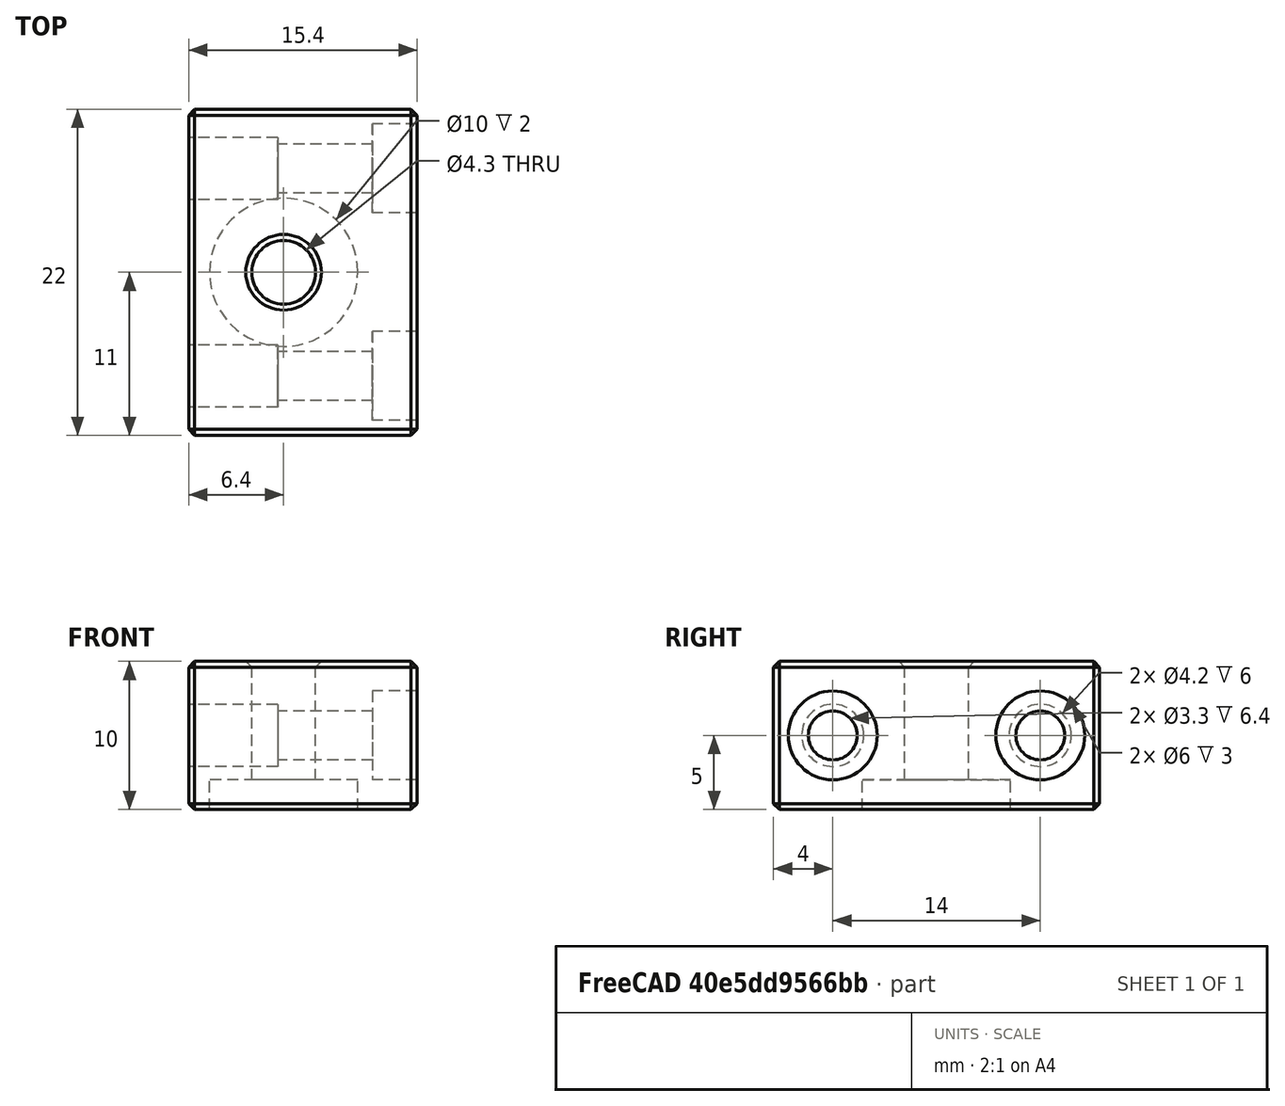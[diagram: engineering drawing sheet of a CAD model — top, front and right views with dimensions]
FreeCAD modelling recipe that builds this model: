
FCSTD DOCUMENT  (FreeCAD 0.18R16146 (Git))
Label: carrier-CF-adjust-block
License: Other
LicenseURL: GPL3
objects: Part::Cylinder×8, Part::Cut×5, Part::MultiFuse×3, Part::Box×1, Part::Chamfer×1
note: 18 computed .brp shape members not serialized (recipe doc carries the construction recipe); baked Part::Feature solids carry a one-line shape summary decoded from their .brp

FEATURE [Part::Box] Box  label="Cube"
  AttacherType = Attacher::AttachEngine3D
  Height = 10
  Length = 15.4
  Placement = pos=(-6.4,-11,0) rot=(0,0,1;0rad)
  Width = 22
FEATURE [Part::Cylinder] Cylinder
  Angle = 360
  AttacherType = Attacher::AttachEngine3D
  Height = 10
  Radius = 2.15
FEATURE [Part::Cylinder] Cylinder001
  Angle = 360
  AttacherType = Attacher::AttachEngine3D
  Height = 2
  Radius = 5
FEATURE [Part::Cylinder] Cylinder002
  Angle = 360
  AttacherType = Attacher::AttachEngine3D
  Height = 16
  Placement = pos=(9,-7,5) rot=(0,1,0;4.71239rad)
  Radius = 1.65
FEATURE [Part::Cylinder] Cylinder003
  Angle = 360
  AttacherType = Attacher::AttachEngine3D
  Height = 16
  Placement = pos=(9,7,5) rot=(0,-1,0;1.5708rad)
  Radius = 1.65
FEATURE [Part::Cylinder] Cylinder004
  Angle = 360
  AttacherType = Attacher::AttachEngine3D
  Height = 6
  Placement = pos=(9,7,5) rot=(0,-1,0;1.5708rad)
  Radius = 2.1
FEATURE [Part::Cylinder] Cylinder005
  Angle = 360
  AttacherType = Attacher::AttachEngine3D
  Height = 6
  Placement = pos=(9,-7,5) rot=(0,-1,0;1.5708rad)
  Radius = 2.1
FEATURE [Part::Cylinder] Cylinder006
  Angle = 360
  AttacherType = Attacher::AttachEngine3D
  Height = 3
  Placement = pos=(9,7,5) rot=(0,-1,0;1.5708rad)
  Radius = 3
FEATURE [Part::Cylinder] Cylinder007
  Angle = 360
  AttacherType = Attacher::AttachEngine3D
  Height = 3
  Placement = pos=(9,-7,5) rot=(0,-1,0;1.5708rad)
  Radius = 3
FEATURE [Part::MultiFuse] Fusion
  Shapes = -> [Cylinder003,Cylinder002]
FEATURE [Part::Cut] Cut
  Base = -> Box
  Tool = -> Fusion
FEATURE [Part::MultiFuse] Fusion001
  Shapes = -> [Cylinder007,Cylinder006]
FEATURE [Part::Cut] Cut001
  Base = -> Cut
  Tool = -> Fusion001
FEATURE [Part::MultiFuse] Fusion002
  Placement = pos=(-9.4,0,0) rot=(0,0,1;0rad)
  Shapes = -> [Cylinder005,Cylinder004]
FEATURE [Part::Cut] Cut002
  Base = -> Cut001
  Tool = -> Fusion002
FEATURE [Part::Cut] Cut003
  Base = -> Cut002
  Tool = -> Cylinder
FEATURE [Part::Cut] Cut004
  Base = -> Cut003
  Tool = -> Cylinder001
FEATURE [Part::Chamfer] Chamfer
  Base = -> Cut004
  Edges = 13 edges r=0.4: [Edge1,Edge2,Edge3,Edge4,Edge7,Edge8,Edge9,Edge10,Edge11,Edge12,Edge13,Edge14,Edge16]
